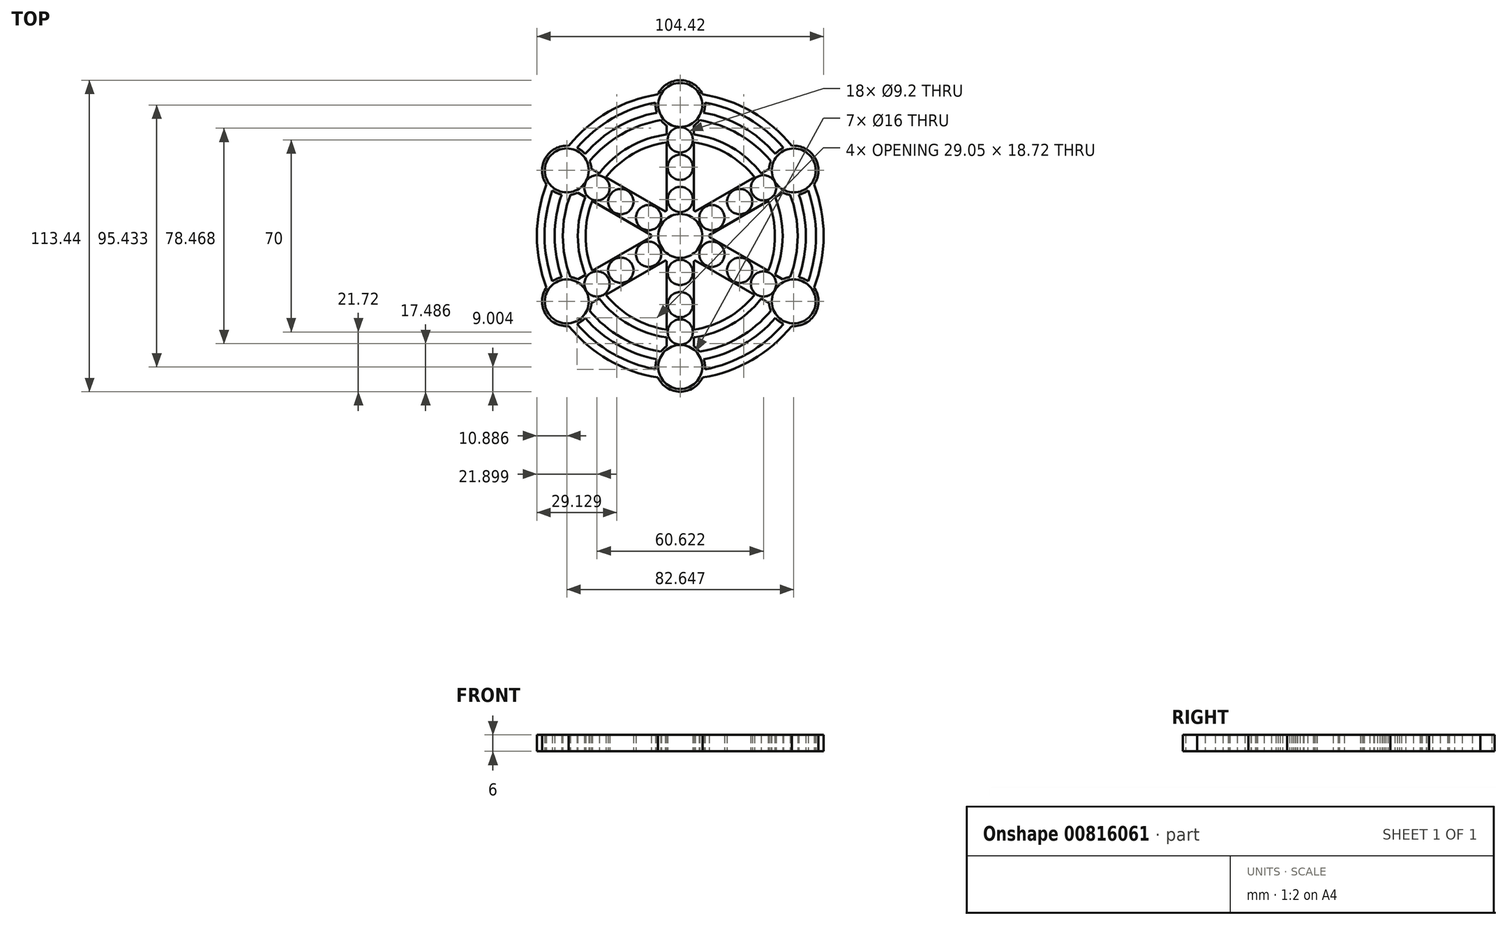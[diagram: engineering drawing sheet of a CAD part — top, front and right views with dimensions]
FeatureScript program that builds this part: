
annotation { "Feature Type Name" : "Feature", "Feature Type Description" : "" }
export const myFeature = defineFeature(function(context is Context, id is Id, definition is map)
    precondition{}
    {
        {
            var Q0;
            Q0=qCreatedBy(makeId("Top.planeOp"),FACE);
            var sketch = newSketch(context, id + "F0", { "sketchPlane" : qUnion([Q0])});
            skCircle(sketch, "E0", {"center": v(0, 0) * mm, "radius": 8 * mm});
            skArc(sketch, "E1", {"start": v(-5, 9.23) * mm, "mid": v(-5.25, 9.1) * mm, "end": v(-5.5, 8.95) * mm});
            skCircle(sketch, "E2", {"center": v(0, 25) * mm, "radius": 4.6 * mm});
            skCircle(sketch, "E3", {"center": v(0, 35) * mm, "radius": 4.6 * mm});
            skLineSegment(sketch, "E4", {"start": v(-5, 40.23) * mm, "end": v(-5, 36.95) * mm});
            skLineSegment(sketch, "E5", {"start": v(5, 40.23) * mm, "end": v(5, 36.95) * mm});
            skArc(sketch, "E6", {"start": v(5, 40.23) * mm, "mid": v(6.12, 41.12) * mm, "end": v(7.09, 42.17) * mm});
            skCircle(sketch, "E7", {"center": v(0, 47.72) * mm, "radius": 8 * mm});
            skPoint(sketch, "E8.orphan", {"position": v(0, 50.46) * mm});
            skCircle(sketch, "E9", {"center": v(0, 13.3) * mm, "radius": 4.6 * mm});
            skLineSegment(sketch, "E10.1.0", {"start": v(-32.34, 24.45) * mm, "end": v(-29.5, 22.8) * mm});
            skLineSegment(sketch, "E10.1.1", {"start": v(-37.34, 15.79) * mm, "end": v(-34.5, 14.14) * mm});
            skCircle(sketch, "E10.1.2", {"center": v(-11.51, 6.65) * mm, "radius": 4.6 * mm});
            skCircle(sketch, "E10.1.3", {"center": v(-21.65, 12.5) * mm, "radius": 4.6 * mm});
            skCircle(sketch, "E10.1.4", {"center": v(-30.31, 17.5) * mm, "radius": 4.6 * mm});
            skArc(sketch, "E10.1.5", {"start": v(-32.34, 24.45) * mm, "mid": v(-32.55, 25.86) * mm, "end": v(-32.98, 27.22) * mm});
            skCircle(sketch, "E10.1.6", {"center": v(-41.32, 23.86) * mm, "radius": 8 * mm});
            skLineSegment(sketch, "E10.2.0", {"start": v(-37.34, -15.79) * mm, "end": v(-34.5, -14.14) * mm});
            skLineSegment(sketch, "E10.2.1", {"start": v(-32.34, -24.45) * mm, "end": v(-29.5, -22.8) * mm});
            skCircle(sketch, "E10.2.2", {"center": v(-11.51, -6.65) * mm, "radius": 4.6 * mm});
            skCircle(sketch, "E10.2.3", {"center": v(-21.65, -12.5) * mm, "radius": 4.6 * mm});
            skCircle(sketch, "E10.2.4", {"center": v(-30.31, -17.5) * mm, "radius": 4.6 * mm});
            skArc(sketch, "E10.2.5", {"start": v(-37.34, -15.79) * mm, "mid": v(-38.67, -15.26) * mm, "end": v(-40.06, -14.95) * mm});
            skCircle(sketch, "E10.2.6", {"center": v(-41.32, -23.86) * mm, "radius": 8 * mm});
            skLineSegment(sketch, "E10.3.0", {"start": v(-5, -40.23) * mm, "end": v(-5, -36.95) * mm});
            skLineSegment(sketch, "E10.3.1", {"start": v(5, -40.23) * mm, "end": v(5, -36.95) * mm});
            skCircle(sketch, "E10.3.2", {"center": v(0, -13.3) * mm, "radius": 4.6 * mm});
            skCircle(sketch, "E10.3.3", {"center": v(0, -25) * mm, "radius": 4.6 * mm});
            skCircle(sketch, "E10.3.4", {"center": v(0, -35) * mm, "radius": 4.6 * mm});
            skArc(sketch, "E10.3.5", {"start": v(-5, -40.23) * mm, "mid": v(-6.12, -41.12) * mm, "end": v(-7.09, -42.17) * mm});
            skCircle(sketch, "E10.3.6", {"center": v(0, -47.72) * mm, "radius": 8 * mm});
            skLineSegment(sketch, "E10.4.0", {"start": v(32.34, -24.45) * mm, "end": v(29.5, -22.8) * mm});
            skLineSegment(sketch, "E10.4.1", {"start": v(37.34, -15.79) * mm, "end": v(34.5, -14.14) * mm});
            skCircle(sketch, "E10.4.2", {"center": v(11.51, -6.65) * mm, "radius": 4.6 * mm});
            skCircle(sketch, "E10.4.3", {"center": v(21.65, -12.5) * mm, "radius": 4.6 * mm});
            skCircle(sketch, "E10.4.4", {"center": v(30.31, -17.5) * mm, "radius": 4.6 * mm});
            skArc(sketch, "E10.4.5", {"start": v(32.34, -24.45) * mm, "mid": v(32.55, -25.86) * mm, "end": v(32.98, -27.22) * mm});
            skCircle(sketch, "E10.4.6", {"center": v(41.32, -23.86) * mm, "radius": 8 * mm});
            skLineSegment(sketch, "E10.5.0", {"start": v(37.34, 15.79) * mm, "end": v(34.5, 14.14) * mm});
            skLineSegment(sketch, "E10.5.1", {"start": v(32.34, 24.45) * mm, "end": v(29.5, 22.8) * mm});
            skCircle(sketch, "E10.5.2", {"center": v(11.51, 6.65) * mm, "radius": 4.6 * mm});
            skCircle(sketch, "E10.5.3", {"center": v(21.65, 12.5) * mm, "radius": 4.6 * mm});
            skCircle(sketch, "E10.5.4", {"center": v(30.31, 17.5) * mm, "radius": 4.6 * mm});
            skArc(sketch, "E10.5.5", {"start": v(37.34, 15.79) * mm, "mid": v(38.67, 15.26) * mm, "end": v(40.06, 14.95) * mm});
            skCircle(sketch, "E10.5.6", {"center": v(41.32, 23.86) * mm, "radius": 8 * mm});
            skArc(sketch, "E11.trimOffspring", {"start": v(-10.5, 0.29) * mm, "mid": v(-10.5, 0) * mm, "end": v(-10.5, -0.29) * mm});
            skArc(sketch, "E12.trimOffspring", {"start": v(5.5, 8.95) * mm, "mid": v(5.25, 9.1) * mm, "end": v(5, 9.23) * mm});
            skArc(sketch, "E13.trimOffspring", {"start": v(10.5, -0.29) * mm, "mid": v(10.5, 0) * mm, "end": v(10.5, 0.29) * mm});
            skArc(sketch, "E14.trimOffspring", {"start": v(5, -9.23) * mm, "mid": v(6.07, -8.57) * mm, "end": v(7.05, -7.78) * mm});
            skArc(sketch, "E15.trimOffspring", {"start": v(-5.5, -8.95) * mm, "mid": v(-5.25, -9.1) * mm, "end": v(-5, -9.23) * mm});
            skArc(sketch, "E16", {"start": v(-8.13, 51.57) * mm, "mid": v(-26.1, 45.21) * mm, "end": v(-40.6, 32.83) * mm});
            skArc(sketch, "E17", {"start": v(-8.96, 48.6) * mm, "mid": v(-24.7, 42.8) * mm, "end": v(-37.6, 32.05) * mm});
            skArc(sketch, "E18", {"start": v(-8.56, 44.93) * mm, "mid": v(-22.87, 39.6) * mm, "end": v(-34.63, 29.87) * mm});
            skArc(sketch, "E19", {"start": v(-7.09, 42.17) * mm, "mid": v(-21.38, 37.03) * mm, "end": v(-32.98, 27.22) * mm});
            skArc(sketch, "E20", {"start": v(29.5, 22.8) * mm, "mid": v(18.64, 32.29) * mm, "end": v(5, 36.95) * mm});
            skArc(sketch, "E21", {"start": v(27.04, 21.38) * mm, "mid": v(17.23, 29.85) * mm, "end": v(5, 34.1) * mm});
            skArc(sketch, "E22.trimOffspring", {"start": v(8.13, 51.57) * mm, "mid": v(0, 56.72) * mm, "end": v(-8.13, 51.57) * mm});
            skArc(sketch, "E23.trimOffspring", {"start": v(-8.96, 48.6) * mm, "mid": v(-8.95, 46.74) * mm, "end": v(-8.56, 44.93) * mm});
            skArc(sketch, "E24.trimOffspring", {"start": v(-7.09, 42.17) * mm, "mid": v(-6.12, 41.12) * mm, "end": v(-5, 40.23) * mm});
            skArc(sketch, "E25.trimOffspring", {"start": v(40.6, 32.83) * mm, "mid": v(26.1, 45.21) * mm, "end": v(8.13, 51.57) * mm});
            skArc(sketch, "E26.trimOffspring", {"start": v(37.6, 32.05) * mm, "mid": v(24.7, 42.8) * mm, "end": v(8.96, 48.6) * mm});
            skArc(sketch, "E27.trimOffspring", {"start": v(34.63, 29.87) * mm, "mid": v(22.87, 39.6) * mm, "end": v(8.56, 44.93) * mm});
            skArc(sketch, "E28.trimOffspring", {"start": v(32.98, 27.22) * mm, "mid": v(21.38, 37.03) * mm, "end": v(7.09, 42.17) * mm});
            skArc(sketch, "E29.trimOffspring", {"start": v(43.19, 15.05) * mm, "mid": v(44.95, 15.62) * mm, "end": v(46.56, 16.54) * mm});
            skArc(sketch, "E30.trimOffspring", {"start": v(48.73, 18.74) * mm, "mid": v(49.12, 28.36) * mm, "end": v(40.6, 32.83) * mm});
            skArc(sketch, "E31.trimOffspring", {"start": v(32.98, 27.22) * mm, "mid": v(32.55, 25.86) * mm, "end": v(32.34, 24.45) * mm});
            skArc(sketch, "E32.trimOffspring", {"start": v(37.6, 32.05) * mm, "mid": v(36, 31.12) * mm, "end": v(34.63, 29.87) * mm});
            skArc(sketch, "E33.MirrorCS", {"start": v(8.96, 48.6) * mm, "mid": v(8.95, 46.74) * mm, "end": v(8.56, 44.93) * mm});
            skArc(sketch, "E34.trimOffspring", {"start": v(32.04, -12.72) * mm, "mid": v(34.47, 0) * mm, "end": v(32.04, 12.72) * mm});
            skArc(sketch, "E35.trimOffspring", {"start": v(34.5, -14.14) * mm, "mid": v(37.29, 0) * mm, "end": v(34.5, 14.14) * mm});
            skLineSegment(sketch, "E36.trimOffspring", {"start": v(32.04, -12.72) * mm, "end": v(10.5, -0.29) * mm});
            skLineSegment(sketch, "E37.trimOffspring", {"start": v(32.04, 12.72) * mm, "end": v(10.5, 0.29) * mm});
            skLineSegment(sketch, "E38.trimOffspring", {"start": v(27.04, 21.38) * mm, "end": v(5.5, 8.95) * mm});
            skArc(sketch, "E39.trimOffspring", {"start": v(40.06, -14.95) * mm, "mid": v(42.76, 0) * mm, "end": v(40.06, 14.95) * mm});
            skArc(sketch, "E40.trimOffspring", {"start": v(43.19, -15.05) * mm, "mid": v(45.73, 0) * mm, "end": v(43.19, 15.05) * mm});
            skArc(sketch, "E41.trimOffspring", {"start": v(46.56, -16.54) * mm, "mid": v(49.41, 0) * mm, "end": v(46.56, 16.54) * mm});
            skArc(sketch, "E42.trimOffspring", {"start": v(48.73, -18.74) * mm, "mid": v(52.2, 0) * mm, "end": v(48.73, 18.74) * mm});
            skArc(sketch, "E43.trimOffspring", {"start": v(46.56, -16.54) * mm, "mid": v(44.95, -15.62) * mm, "end": v(43.19, -15.05) * mm});
            skArc(sketch, "E44.trimOffspring", {"start": v(40.06, -14.95) * mm, "mid": v(38.67, -15.26) * mm, "end": v(37.34, -15.79) * mm});
            skArc(sketch, "E45.trimOffspring", {"start": v(40.6, -32.83) * mm, "mid": v(49.12, -28.36) * mm, "end": v(48.73, -18.74) * mm});
            skArc(sketch, "E46.trimOffspring", {"start": v(34.63, -29.87) * mm, "mid": v(36, -31.12) * mm, "end": v(37.6, -32.05) * mm});
            skLineSegment(sketch, "E47.trimOffspring", {"start": v(27.04, -21.38) * mm, "end": v(5.5, -8.95) * mm});
            skLineSegment(sketch, "E48.trimOffspring", {"start": v(5, 34.1) * mm, "end": v(5, 9.23) * mm});
            skArc(sketch, "E49.trimOffspring", {"start": v(-5, 36.95) * mm, "mid": v(-18.64, 32.29) * mm, "end": v(-29.5, 22.8) * mm});
            skArc(sketch, "E50.trimOffspring", {"start": v(-5, 34.1) * mm, "mid": v(-17.23, 29.85) * mm, "end": v(-27.04, 21.38) * mm});
            skLineSegment(sketch, "E51.trimOffspring", {"start": v(-5, 34.1) * mm, "end": v(-5, 9.23) * mm});
            skArc(sketch, "E52.trimOffspring", {"start": v(-32.04, 12.72) * mm, "mid": v(-34.47, 0) * mm, "end": v(-32.04, -12.72) * mm});
            skArc(sketch, "E53.trimOffspring", {"start": v(-34.5, 14.14) * mm, "mid": v(-37.29, 0) * mm, "end": v(-34.5, -14.14) * mm});
            skArc(sketch, "E54.trimOffspring", {"start": v(-40.06, 14.95) * mm, "mid": v(-42.76, 0) * mm, "end": v(-40.06, -14.95) * mm});
            skArc(sketch, "E55.trimOffspring", {"start": v(-43.19, 15.05) * mm, "mid": v(-45.73, 0) * mm, "end": v(-43.19, -15.05) * mm});
            skArc(sketch, "E56.trimOffspring", {"start": v(-46.56, 16.54) * mm, "mid": v(-49.41, 0) * mm, "end": v(-46.56, -16.54) * mm});
            skArc(sketch, "E57.trimOffspring", {"start": v(-48.73, 18.74) * mm, "mid": v(-52.2, 0) * mm, "end": v(-48.73, -18.74) * mm});
            skArc(sketch, "E58.trimOffspring", {"start": v(-40.6, 32.83) * mm, "mid": v(-49.12, 28.36) * mm, "end": v(-48.73, 18.74) * mm});
            skArc(sketch, "E59.trimOffspring", {"start": v(-34.63, 29.87) * mm, "mid": v(-36, 31.12) * mm, "end": v(-37.6, 32.05) * mm});
            skLineSegment(sketch, "E60.trimOffspring", {"start": v(-27.04, 21.38) * mm, "end": v(-5.5, 8.95) * mm});
            skArc(sketch, "E61.trimOffspring", {"start": v(-46.56, 16.54) * mm, "mid": v(-44.95, 15.62) * mm, "end": v(-43.19, 15.05) * mm});
            skArc(sketch, "E62.trimOffspring", {"start": v(-40.06, 14.95) * mm, "mid": v(-38.67, 15.26) * mm, "end": v(-37.34, 15.79) * mm});
            skLineSegment(sketch, "E63.trimOffspring", {"start": v(-32.04, 12.72) * mm, "end": v(-10.5, 0.29) * mm});
            skArc(sketch, "E64.trimOffspring", {"start": v(-48.73, -18.74) * mm, "mid": v(-49.12, -28.36) * mm, "end": v(-40.6, -32.83) * mm});
            skArc(sketch, "E65.trimOffspring", {"start": v(-40.6, -32.83) * mm, "mid": v(-26.1, -45.21) * mm, "end": v(-8.13, -51.57) * mm});
            skArc(sketch, "E66.trimOffspring", {"start": v(-37.6, -32.05) * mm, "mid": v(-24.7, -42.8) * mm, "end": v(-8.96, -48.6) * mm});
            skArc(sketch, "E67.trimOffspring", {"start": v(-34.63, -29.87) * mm, "mid": v(-22.87, -39.6) * mm, "end": v(-8.56, -44.93) * mm});
            skArc(sketch, "E68.trimOffspring", {"start": v(-32.98, -27.22) * mm, "mid": v(-21.38, -37.03) * mm, "end": v(-7.09, -42.17) * mm});
            skArc(sketch, "E69.trimOffspring", {"start": v(-29.5, -22.8) * mm, "mid": v(-18.64, -32.29) * mm, "end": v(-5, -36.95) * mm});
            skArc(sketch, "E70.trimOffspring", {"start": v(-27.04, -21.38) * mm, "mid": v(-17.23, -29.85) * mm, "end": v(-5, -34.1) * mm});
            skLineSegment(sketch, "E71.trimOffspring", {"start": v(-32.04, -12.72) * mm, "end": v(-10.5, -0.29) * mm});
            skLineSegment(sketch, "E72.trimOffspring", {"start": v(-27.04, -21.38) * mm, "end": v(-5.5, -8.95) * mm});
            skArc(sketch, "E73.trimOffspring", {"start": v(-37.6, -32.05) * mm, "mid": v(-36, -31.12) * mm, "end": v(-34.63, -29.87) * mm});
            skArc(sketch, "E74.trimOffspring", {"start": v(-32.98, -27.22) * mm, "mid": v(-32.55, -25.86) * mm, "end": v(-32.34, -24.45) * mm});
            skArc(sketch, "E75.trimOffspring", {"start": v(-43.19, -15.05) * mm, "mid": v(-44.95, -15.62) * mm, "end": v(-46.56, -16.54) * mm});
            skArc(sketch, "E76.trimOffspring", {"start": v(5, -34.1) * mm, "mid": v(17.23, -29.85) * mm, "end": v(27.04, -21.38) * mm});
            skArc(sketch, "E77.trimOffspring", {"start": v(5, -36.95) * mm, "mid": v(18.64, -32.29) * mm, "end": v(29.5, -22.8) * mm});
            skArc(sketch, "E78.trimOffspring", {"start": v(7.09, -42.17) * mm, "mid": v(21.38, -37.03) * mm, "end": v(32.98, -27.22) * mm});
            skArc(sketch, "E79.trimOffspring", {"start": v(8.56, -44.93) * mm, "mid": v(22.87, -39.6) * mm, "end": v(34.63, -29.87) * mm});
            skArc(sketch, "E80.trimOffspring", {"start": v(8.96, -48.6) * mm, "mid": v(24.7, -42.8) * mm, "end": v(37.6, -32.05) * mm});
            skArc(sketch, "E81.trimOffspring", {"start": v(8.13, -51.57) * mm, "mid": v(26.1, -45.21) * mm, "end": v(40.6, -32.83) * mm});
            skArc(sketch, "E82.trimOffspring", {"start": v(-8.13, -51.57) * mm, "mid": v(0, -56.72) * mm, "end": v(8.13, -51.57) * mm});
            skArc(sketch, "E83.trimOffspring", {"start": v(-8.56, -44.93) * mm, "mid": v(-8.95, -46.74) * mm, "end": v(-8.96, -48.6) * mm});
            skArc(sketch, "E84.trimOffspring", {"start": v(7.09, -42.17) * mm, "mid": v(6.12, -41.12) * mm, "end": v(5, -40.23) * mm});
            skArc(sketch, "E85.trimOffspring", {"start": v(8.96, -48.6) * mm, "mid": v(8.95, -46.74) * mm, "end": v(8.56, -44.93) * mm});
            skLineSegment(sketch, "E86.trimOffspring", {"start": v(-5, -34.1) * mm, "end": v(-5, -9.23) * mm});
            skLineSegment(sketch, "E87.trimOffspring", {"start": v(5, -34.1) * mm, "end": v(5, -9.23) * mm});
            skSolve(sketch);
        }
        {
            var Q0;
            Q0 = qSketchRegion(id + "F0", true);
            extrude(context, id + "F1", {"entities" : qUnion([Q0]), "depth" : 6 * mm, "offsetDistance" : 25 * mm});
        }
    });
